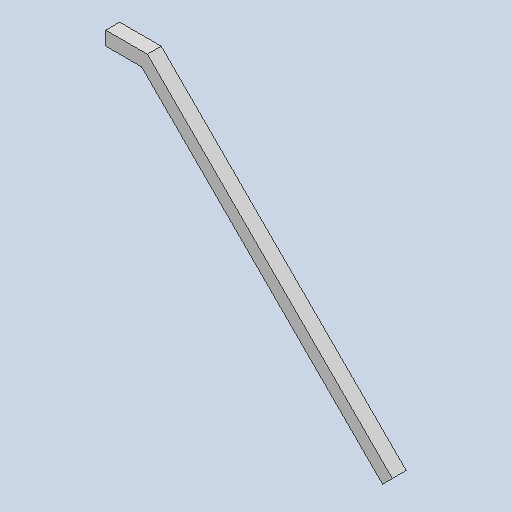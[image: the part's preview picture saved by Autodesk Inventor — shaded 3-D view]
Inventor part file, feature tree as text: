
AUTODESK INVENTOR PART (.ipt)
format: ipt  version: 2023 (Build 270158030, 158C)  size: 100,352 bytes
history: native  units: in
note: dims shown in document units (in); Inventor stores cm internally (conversion verified against a paired STEP export)
features: extrude x3, sketch x1
ambient origin geometry x8: Origin, YZ Plane, XZ Plane, XY Plane, X Axis, Y Axis, Z Axis, Center Point
bodies: Solid1 (feature_tree)
feature tree (4):
  sketch  "Sketch1"  dims[d0=12.5in d1=135.0deg d2=1.5in d3=0.5in d5=0.5in d6=90.0deg d7=0.0625in d8=0.0in d9=0.0625in d10=0.0625in d11=90.0deg d14=0.4375in d15=0.0in d16=0.4375in d17=0.0in]
  extrude  "Extrusion1"  TaperAngle=135.0deg  [1 undecoded]
  extrude  "Extrusion3"  Depth=0.4375in
  extrude  "Extrusion4"  Depth=0.5in
note: 1 required parameter value undecoded (feature->parameter linkage not recoverable at this tier; creation-order binding heuristic only, values carry confidence <= 0.55)
